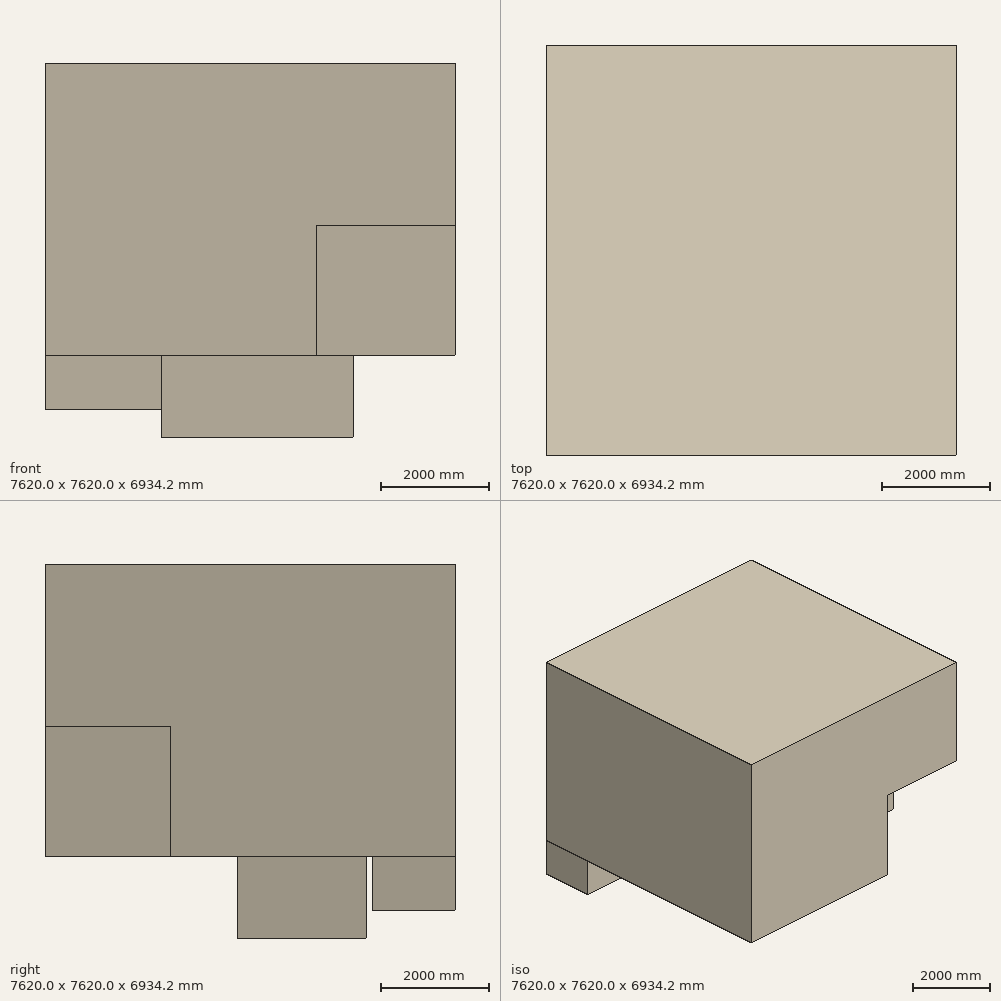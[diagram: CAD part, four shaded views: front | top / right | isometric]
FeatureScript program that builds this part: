
annotation { "Feature Type Name" : "Feature", "Feature Type Description" : "" }
export const myFeature = defineFeature(function(context is Context, id is Id, definition is map)
    precondition{}
    {
        {
            var Q0;
            Q0=qCreatedBy(makeId("Top.planeOp"),FACE);
            var sketch = newSketch(context, id + "F0", { "sketchPlane" : qUnion([Q0])});
            skLineSegment(sketch, "E0.bottom", {"start": v(-3806.85, 4707.99) * mm, "end": v(3813.15, 4707.99) * mm});
            skLineSegment(sketch, "E0.top", {"start": v(-3806.85, -2912.01) * mm, "end": v(3813.15, -2912.01) * mm});
            skLineSegment(sketch, "E0.left", {"start": v(-3806.85, 4707.99) * mm, "end": v(-3806.85, -2912.01) * mm});
            skLineSegment(sketch, "E0.right", {"start": v(3813.15, 4707.99) * mm, "end": v(3813.15, -2912.01) * mm});
            skSolve(sketch);
        }
        {
            var Q0;
            Q0=makeQuery(id+"F0.imprint","IMPRINT",FACE,{"disambiguationData":[TD([[makeQuery(id+"F0.imprint","IMPRINT",EDGE,{"derivedFrom":sQuery(id+"F0.wireOp",EDGE,"E0.bottom")}),-1.0]])]});
            extrude(context, id + "F1", {"entities" : qUnion([Q0]), "depth" : 5410.2 * mm, "offsetDistance" : 25.4 * mm});
        }
        {
            var Q0;
            Q0=makeQuery(id+"F1.opExtrude","CAP_FACE",FACE,{"disambiguationData":[OSD([sQuery(id+"F0.wireOp",EDGE,"E0.bottom"),sQuery(id+"F0.wireOp",EDGE,"E0.top"),sQuery(id+"F0.wireOp",EDGE,"E0.left"),sQuery(id+"F0.wireOp",EDGE,"E0.right")])],"isStart":true});
            var sketch = newSketch(context, id + "F2", { "sketchPlane" : qUnion([Q0])});
            skLineSegment(sketch, "E1.bottom", {"start": v(3813.15, 2912.01) * mm, "end": v(1230.78, 2912.01) * mm});
            skLineSegment(sketch, "E1.top", {"start": v(3813.15, 586.66) * mm, "end": v(1230.78, 586.66) * mm});
            skLineSegment(sketch, "E1.left", {"start": v(3813.15, 2912.01) * mm, "end": v(3813.15, 586.66) * mm});
            skLineSegment(sketch, "E1.right", {"start": v(1230.78, 2912.01) * mm, "end": v(1230.78, 586.66) * mm});
            skSolve(sketch);
        }
        {
            var Q0;
            Q0 = qSketchRegion(id + "F2", true);
            extrude(context, id + "F3", {"entities" : qUnion([Q0]), "operationType" : NewBodyOperationType.REMOVE, "oppositeDirection" : true, "depth" : 2413 * mm, "offsetDistance" : 25.4 * mm});
        }
        {
            var Q0;
            Q0=makeQuery(id+"F1.opExtrude","CAP_FACE",FACE,{"disambiguationData":[OSD([sQuery(id+"F0.wireOp",EDGE,"E0.bottom"),sQuery(id+"F0.wireOp",EDGE,"E0.top"),sQuery(id+"F0.wireOp",EDGE,"E0.left"),sQuery(id+"F0.wireOp",EDGE,"E0.right")])],"isStart":true});
            var sketch = newSketch(context, id + "F4", { "sketchPlane" : qUnion([Q0])});
            skLineSegment(sketch, "E2.bottom", {"start": v(-1651.33, -665.26) * mm, "end": v(1919.97, -665.26) * mm});
            skLineSegment(sketch, "E2.top", {"start": v(-1651.33, -3051.77) * mm, "end": v(1919.97, -3051.77) * mm});
            skLineSegment(sketch, "E2.left", {"start": v(-1651.33, -665.26) * mm, "end": v(-1651.33, -3051.77) * mm});
            skLineSegment(sketch, "E2.right", {"start": v(1919.97, -665.26) * mm, "end": v(1919.97, -3051.77) * mm});
            skSolve(sketch);
        }
        {
            var Q0;
            Q0 = qSketchRegion(id + "F4", true);
            extrude(context, id + "F5", {"entities" : qUnion([Q0]), "depth" : 1524 * mm, "offsetDistance" : 25.4 * mm});
        }
        {
            var Q0;
            Q0=makeQuery(id+"F1.opExtrude","CAP_FACE",FACE,{"disambiguationData":[OSD([sQuery(id+"F0.wireOp",EDGE,"E0.bottom"),sQuery(id+"F0.wireOp",EDGE,"E0.top"),sQuery(id+"F0.wireOp",EDGE,"E0.left"),sQuery(id+"F0.wireOp",EDGE,"E0.right")])],"isStart":true});
            var sketch = newSketch(context, id + "F6", { "sketchPlane" : qUnion([Q0])});
            skLineSegment(sketch, "E3.bottom", {"start": v(-3806.85, -3170.85) * mm, "end": v(-1565.99, -3170.85) * mm});
            skLineSegment(sketch, "E3.top", {"start": v(-3806.85, -4707.99) * mm, "end": v(-1565.99, -4707.99) * mm});
            skLineSegment(sketch, "E3.left", {"start": v(-3806.85, -3170.85) * mm, "end": v(-3806.85, -4707.99) * mm});
            skLineSegment(sketch, "E3.right", {"start": v(-1565.99, -3170.85) * mm, "end": v(-1565.99, -4707.99) * mm});
            skSolve(sketch);
        }
        {
            var Q0;
            Q0 = qSketchRegion(id + "F6", true);
            extrude(context, id + "F7", {"entities" : qUnion([Q0]), "depth" : 1016 * mm, "offsetDistance" : 25.4 * mm});
        }
    });
